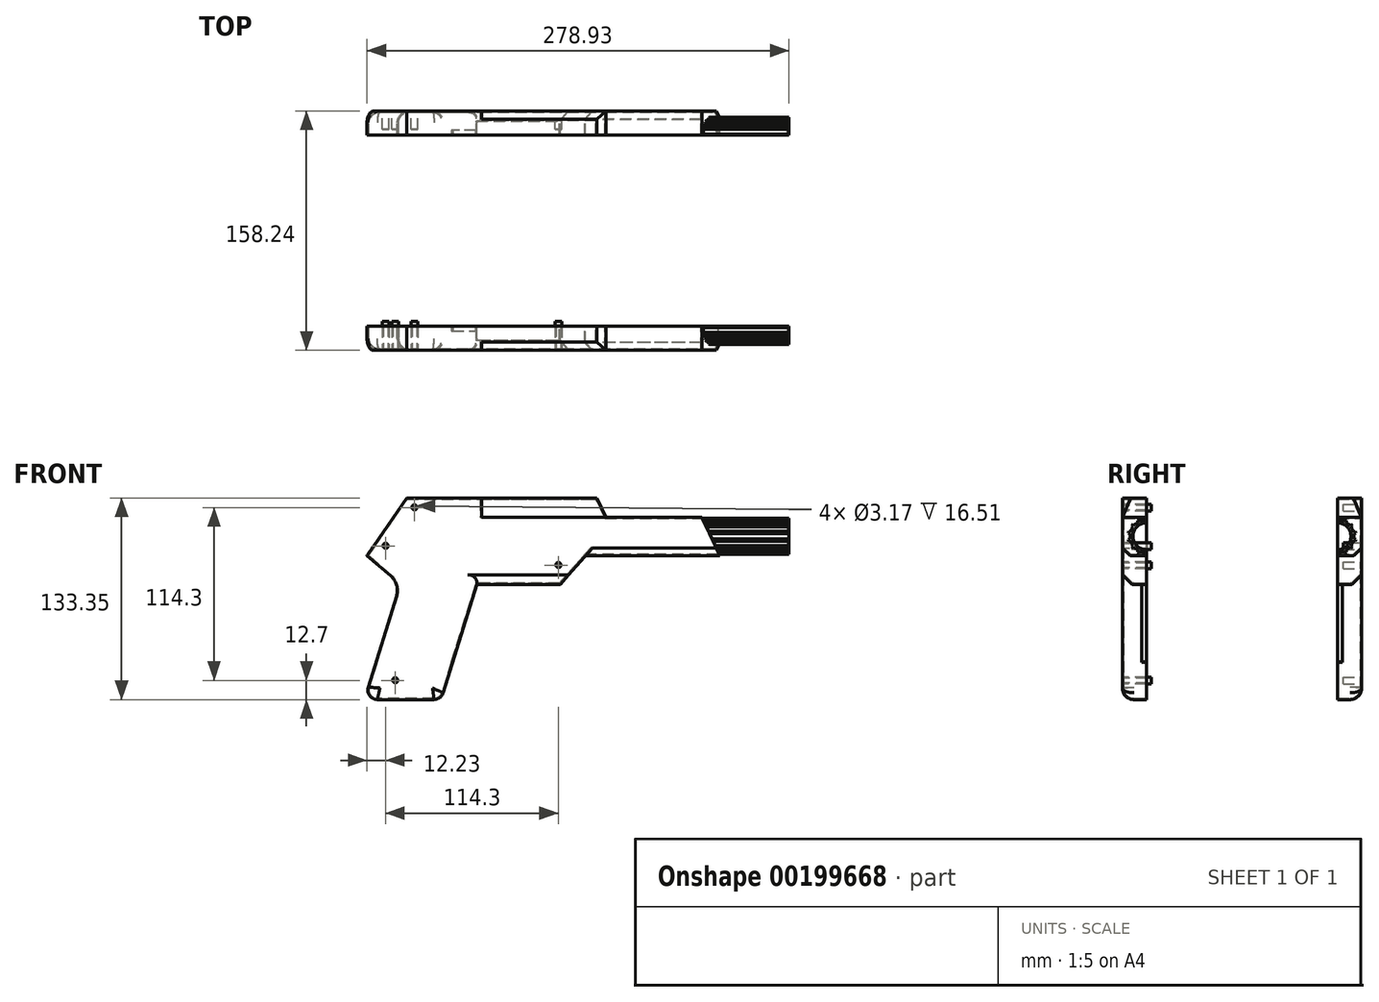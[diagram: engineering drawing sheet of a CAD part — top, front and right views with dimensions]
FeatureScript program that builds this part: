
annotation { "Feature Type Name" : "Feature", "Feature Type Description" : "" }
export const myFeature = defineFeature(function(context is Context, id is Id, definition is map)
    precondition{}
    {
        {
            var Q0;
            Q0=qCreatedBy(makeId("Front.planeOp"),FACE);
            var sketch = newSketch(context, id + "F0", { "sketchPlane" : qUnion([Q0])});
            skLineSegment(sketch, "E0", {"start": v(-151.93, 19.05) * mm, "end": v(-125.83, 57.15) * mm});
            skLineSegment(sketch, "E1", {"start": v(-125.83, 57.15) * mm, "end": v(0, 57.15) * mm});
            skLineSegment(sketch, "E2", {"start": v(0, 57.15) * mm, "end": v(6.06, 44.45) * mm});
            skLineSegment(sketch, "E3", {"start": v(6.06, 44.45) * mm, "end": v(69.56, 44.45) * mm});
            skLineSegment(sketch, "E4", {"start": v(69.56, 44.45) * mm, "end": v(81.44, 19.05) * mm});
            skLineSegment(sketch, "E5", {"start": v(81.44, 19.05) * mm, "end": v(-7.46, 19.05) * mm});
            skLineSegment(sketch, "E6", {"start": v(-7.46, 19.05) * mm, "end": v(-24.23, 0) * mm});
            skLineSegment(sketch, "E7", {"start": v(-24.23, 0) * mm, "end": v(-79.23, 0) * mm});
            skLineSegment(sketch, "E8", {"start": v(-79.23, 0) * mm, "end": v(-101.6, -71.74) * mm});
            skLineSegment(sketch, "E9", {"start": v(-107.67, -76.2) * mm, "end": v(-145.17, -76.2) * mm});
            skLineSegment(sketch, "E10", {"start": v(-151.23, -67.96) * mm, "end": v(-132.5, -7.92) * mm});
            skLineSegment(sketch, "E11", {"start": v(-136.29, 5.44) * mm, "end": v(-151.93, 19.05) * mm});
            skPoint(sketch, "E12.visualSharp", {"position": v(-130.03, 0) * mm});
            skArc(sketch, "E12.filletArc", {"start": v(-132.5, -7.92) * mm, "mid": v(-132.4, -0.67) * mm, "end": v(-136.29, 5.44) * mm});
            skPoint(sketch, "E13.visualSharp", {"position": v(-153.8, -76.2) * mm});
            skArc(sketch, "E13.filletArc", {"start": v(-151.23, -67.96) * mm, "mid": v(-150.28, -73.61) * mm, "end": v(-145.17, -76.2) * mm});
            skPoint(sketch, "E14.visualSharp", {"position": v(-103, -76.2) * mm});
            skArc(sketch, "E14.filletArc", {"start": v(-107.67, -76.2) * mm, "mid": v(-103.9, -74.97) * mm, "end": v(-101.6, -71.74) * mm});
            skSolve(sketch);
        }
        {
            var Q0;
            Q0=makeQuery(id+"F0.imprint","IMPRINT",FACE,{"disambiguationData":[TD([[makeQuery(id+"F0.imprint","IMPRINT",EDGE,{"derivedFrom":sQuery(id+"F0.wireOp",EDGE,"E0")}),-1.0]])]});
            extrude(context, id + "F1", {"entities" : qUnion([Q0]), "depth" : 31.75 * mm});
        }
        {
            var Q0;
            Q0=qCreatedBy(makeId("Right.planeOp"),FACE);
            var sketch = newSketch(context, id + "F2", { "sketchPlane" : qUnion([Q0])});
            skCircle(sketch, "E15", {"center": v(-15.88, 31.75) * mm, "radius": 10.8 * mm});
            skLineSegment(sketch, "E16.0", {"start": v(-31.75, 19.05) * mm, "end": v(0, 19.05) * mm});
            skSolve(sketch);
        }
        {
            var Q0;
            Q0=makeQuery(id+"F2.imprint","IMPRINT",FACE,{"disambiguationData":[TD([[makeQuery(id+"F2.imprint","IMPRINT",EDGE,{"derivedFrom":sQuery(id+"F2.wireOp",EDGE,"E15")}),1.0]])]});
            extrude(context, id + "F3", {"entities" : qUnion([Q0]), "operationType" : NewBodyOperationType.ADD, "depth" : 127 * mm});
        }
        {
            var Q0;
            Q0=makeQuery(id+"F3.opExtrude","CAP_FACE",FACE,{"disambiguationData":[OSD([sQuery(id+"F2.wireOp",EDGE,"E15")])],"isStart":false});
            var sketch = newSketch(context, id + "F4", { "sketchPlane" : qUnion([Q0])});
            skPoint(sketch, "E17.0", {"position": v(-15.88, 57.15) * mm});
            skLineSegment(sketch, "E18.0.0", {"start": v(0, 44.45) * mm, "end": v(0, 57.15) * mm});
            skLineSegment(sketch, "E18.0.1", {"start": v(0, 57.15) * mm, "end": v(-31.75, 57.15) * mm});
            skLineSegment(sketch, "E18.0.2", {"start": v(-31.75, 57.15) * mm, "end": v(-31.75, 44.45) * mm});
            skLineSegment(sketch, "E18.0.3", {"start": v(-31.75, 44.45) * mm, "end": v(0, 44.45) * mm});
            skLineSegment(sketch, "E19", {"start": v(-31.75, 44.45) * mm, "end": v(-26.23, 57.15) * mm});
            skLineSegment(sketch, "E20", {"start": v(-15.88, 57.15) * mm, "end": v(-15.88, 44.45) * mm});
            skLineSegment(sketch, "E21.MirrorCS", {"start": v(0, 44.45) * mm, "end": v(-5.52, 57.15) * mm});
            skSolve(sketch);
        }
        {
            var Q0;
            {var subQ0=sQuery(id+"F4.wireOp",EDGE,"E18.0.2");Q0=makeQuery(id+"F4.imprint","IMPRINT",FACE,{"disambiguationData":[TD([[makeQuery(id+"F4.imprint","IMPRINT",EDGE,{"derivedFrom":subQ0}),1.0]])]});}
            var Q1;
            {var subQ0=sQuery(id+"F4.wireOp",EDGE,"E18.0.0");Q1=makeQuery(id+"F4.imprint","IMPRINT",FACE,{"disambiguationData":[TD([[makeQuery(id+"F4.imprint","IMPRINT",EDGE,{"derivedFrom":subQ0}),1.0]])]});}
            extrude(context, id + "F5", {"entities" : qUnion([Q0, Q1]), "operationType" : NewBodyOperationType.REMOVE, "oppositeDirection" : true, "depth" : 203.2 * mm});
        }
        {
            var Q0;
            Q0=makeQuery(id+"F3.opExtrude","CAP_FACE",FACE,{"disambiguationData":[OSD([sQuery(id+"F2.wireOp",EDGE,"E15")])],"isStart":false});
            var sketch = newSketch(context, id + "F6", { "sketchPlane" : qUnion([Q0])});
            skPoint(sketch, "E22.0", {"position": v(0, 0) * mm});
            skLineSegment(sketch, "E23", {"start": v(-15.88, 31.75) * mm, "end": v(-15.88, 13.86) * mm});
            skLineSegment(sketch, "E24", {"start": v(-16.64, 20.98) * mm, "end": v(-16.64, 19.71) * mm});
            skLineSegment(sketch, "E25", {"start": v(-16.64, 19.71) * mm, "end": v(-15.88, 19.71) * mm});
            skLineSegment(sketch, "E26.MirrorCS", {"start": v(-15.11, 20.98) * mm, "end": v(-15.11, 19.71) * mm});
            skLineSegment(sketch, "E27.MirrorCS", {"start": v(-15.11, 19.71) * mm, "end": v(-15.88, 19.71) * mm});
            skLineSegment(sketch, "E28.1.0", {"start": v(-10.52, 22.38) * mm, "end": v(-9.97, 21.23) * mm});
            skLineSegment(sketch, "E28.1.1", {"start": v(-9.97, 21.23) * mm, "end": v(-10.65, 20.9) * mm});
            skLineSegment(sketch, "E28.1.2", {"start": v(-11.34, 20.57) * mm, "end": v(-10.65, 20.9) * mm});
            skLineSegment(sketch, "E28.1.3", {"start": v(-11.89, 21.72) * mm, "end": v(-11.34, 20.57) * mm});
            skLineSegment(sketch, "E28.2.0", {"start": v(-6.98, 25.63) * mm, "end": v(-5.99, 24.84) * mm});
            skLineSegment(sketch, "E28.2.1", {"start": v(-5.99, 24.84) * mm, "end": v(-6.46, 24.24) * mm});
            skLineSegment(sketch, "E28.2.2", {"start": v(-6.94, 23.65) * mm, "end": v(-6.46, 24.24) * mm});
            skLineSegment(sketch, "E28.2.3", {"start": v(-7.93, 24.44) * mm, "end": v(-6.94, 23.65) * mm});
            skLineSegment(sketch, "E28.3.0", {"start": v(-5.2, 30.1) * mm, "end": v(-3.97, 29.81) * mm});
            skLineSegment(sketch, "E28.3.1", {"start": v(-3.97, 29.81) * mm, "end": v(-4.14, 29.07) * mm});
            skLineSegment(sketch, "E28.3.2", {"start": v(-4.3, 28.33) * mm, "end": v(-4.14, 29.07) * mm});
            skLineSegment(sketch, "E28.3.3", {"start": v(-5.55, 28.61) * mm, "end": v(-4.3, 28.33) * mm});
            skLineSegment(sketch, "E28.4.0", {"start": v(-5.55, 34.89) * mm, "end": v(-4.3, 35.17) * mm});
            skLineSegment(sketch, "E28.4.1", {"start": v(-4.3, 35.17) * mm, "end": v(-4.14, 34.43) * mm});
            skLineSegment(sketch, "E28.4.2", {"start": v(-3.97, 33.69) * mm, "end": v(-4.14, 34.43) * mm});
            skLineSegment(sketch, "E28.4.3", {"start": v(-5.2, 33.4) * mm, "end": v(-3.97, 33.69) * mm});
            skLineSegment(sketch, "E28.5.0", {"start": v(-7.93, 39.06) * mm, "end": v(-6.94, 39.85) * mm});
            skLineSegment(sketch, "E28.5.1", {"start": v(-6.94, 39.85) * mm, "end": v(-6.46, 39.26) * mm});
            skLineSegment(sketch, "E28.5.2", {"start": v(-5.99, 38.66) * mm, "end": v(-6.46, 39.26) * mm});
            skLineSegment(sketch, "E28.5.3", {"start": v(-6.98, 37.87) * mm, "end": v(-5.99, 38.66) * mm});
            skLineSegment(sketch, "E28.6.0", {"start": v(-11.89, 41.78) * mm, "end": v(-11.34, 42.93) * mm});
            skLineSegment(sketch, "E28.6.1", {"start": v(-11.34, 42.93) * mm, "end": v(-10.65, 42.6) * mm});
            skLineSegment(sketch, "E28.6.2", {"start": v(-9.97, 42.27) * mm, "end": v(-10.65, 42.6) * mm});
            skLineSegment(sketch, "E28.6.3", {"start": v(-10.52, 41.12) * mm, "end": v(-9.97, 42.27) * mm});
            skLineSegment(sketch, "E28.7.0", {"start": v(-16.64, 42.52) * mm, "end": v(-16.64, 43.79) * mm});
            skLineSegment(sketch, "E28.7.1", {"start": v(-16.64, 43.79) * mm, "end": v(-15.88, 43.79) * mm});
            skLineSegment(sketch, "E28.7.2", {"start": v(-15.11, 43.79) * mm, "end": v(-15.88, 43.79) * mm});
            skLineSegment(sketch, "E28.7.3", {"start": v(-15.11, 42.52) * mm, "end": v(-15.11, 43.79) * mm});
            skLineSegment(sketch, "E28.8.0", {"start": v(-21.23, 41.12) * mm, "end": v(-21.78, 42.27) * mm});
            skLineSegment(sketch, "E28.8.1", {"start": v(-21.78, 42.27) * mm, "end": v(-21.1, 42.6) * mm});
            skLineSegment(sketch, "E28.8.2", {"start": v(-20.41, 42.93) * mm, "end": v(-21.1, 42.6) * mm});
            skLineSegment(sketch, "E28.8.3", {"start": v(-19.86, 41.78) * mm, "end": v(-20.41, 42.93) * mm});
            skLineSegment(sketch, "E28.9.0", {"start": v(-24.77, 37.87) * mm, "end": v(-25.76, 38.66) * mm});
            skLineSegment(sketch, "E28.9.1", {"start": v(-25.76, 38.66) * mm, "end": v(-25.29, 39.26) * mm});
            skLineSegment(sketch, "E28.9.2", {"start": v(-24.81, 39.85) * mm, "end": v(-25.29, 39.26) * mm});
            skLineSegment(sketch, "E28.9.3", {"start": v(-23.82, 39.06) * mm, "end": v(-24.81, 39.85) * mm});
            skLineSegment(sketch, "E28.10.0", {"start": v(-26.54, 33.4) * mm, "end": v(-27.78, 33.69) * mm});
            skLineSegment(sketch, "E28.10.1", {"start": v(-27.78, 33.69) * mm, "end": v(-27.61, 34.43) * mm});
            skLineSegment(sketch, "E28.10.2", {"start": v(-27.44, 35.17) * mm, "end": v(-27.61, 34.43) * mm});
            skLineSegment(sketch, "E28.10.3", {"start": v(-26.2, 34.89) * mm, "end": v(-27.44, 35.17) * mm});
            skLineSegment(sketch, "E28.11.0", {"start": v(-26.2, 28.61) * mm, "end": v(-27.44, 28.33) * mm});
            skLineSegment(sketch, "E28.11.1", {"start": v(-27.44, 28.33) * mm, "end": v(-27.61, 29.07) * mm});
            skLineSegment(sketch, "E28.11.2", {"start": v(-27.78, 29.81) * mm, "end": v(-27.61, 29.07) * mm});
            skLineSegment(sketch, "E28.11.3", {"start": v(-26.54, 30.1) * mm, "end": v(-27.78, 29.81) * mm});
            skLineSegment(sketch, "E28.12.0", {"start": v(-23.82, 24.44) * mm, "end": v(-24.81, 23.65) * mm});
            skLineSegment(sketch, "E28.12.1", {"start": v(-24.81, 23.65) * mm, "end": v(-25.29, 24.24) * mm});
            skLineSegment(sketch, "E28.12.2", {"start": v(-25.76, 24.84) * mm, "end": v(-25.29, 24.24) * mm});
            skLineSegment(sketch, "E28.12.3", {"start": v(-24.77, 25.63) * mm, "end": v(-25.76, 24.84) * mm});
            skLineSegment(sketch, "E28.13.0", {"start": v(-19.86, 21.72) * mm, "end": v(-20.41, 20.57) * mm});
            skLineSegment(sketch, "E28.13.1", {"start": v(-20.41, 20.57) * mm, "end": v(-21.1, 20.9) * mm});
            skLineSegment(sketch, "E28.13.2", {"start": v(-21.78, 21.23) * mm, "end": v(-21.1, 20.9) * mm});
            skLineSegment(sketch, "E28.13.3", {"start": v(-21.23, 22.38) * mm, "end": v(-21.78, 21.23) * mm});
            skPoint(sketch, "E28.center", {"position": v(-15.88, 31.75) * mm});
            skSolve(sketch);
        }
        {
            var Q0;
            Q0=makeQuery(id+"F1.opExtrude","CAP_EDGE",EDGE,{"disambiguationData":[OSD([sQuery(id+"F0.wireOp",EDGE,"E11")])],"isStart":false});
            fillet(context, id + "F7", {"entities" : qUnion([Q0]), "radius" : 7.62 * mm, "tangentPropagation" : true, "allowEdgeOverflow" : false});
        }
        {
            var Q0;
            Q0=makeQuery(id+"F1.opExtrude","CAP_EDGE",EDGE,{"disambiguationData":[OSD([sQuery(id+"F0.wireOp",EDGE,"E8")])],"isStart":true});
            fillet(context, id + "F8", {"entities" : qUnion([Q0]), "radius" : 7.62 * mm, "tangentPropagation" : true, "allowEdgeOverflow" : false});
        }
        {
            var Q0;
            Q0=makeQuery(id+"F1.opExtrude","CAP_EDGE",EDGE,{"disambiguationData":[OSD([sQuery(id+"F0.wireOp",EDGE,"E7")])],"isStart":false});
            var Q1;
            Q1=makeQuery(id+"F1.opExtrude","CAP_EDGE",EDGE,{"disambiguationData":[OSD([sQuery(id+"F0.wireOp",EDGE,"E7")])],"isStart":true});
            chamfer(context, id + "F9", {"entities" : qUnion([Q0, Q1]), "width" : 6.35 * mm, "tangentPropagation" : true});
        }
        {
            var Q0;
            Q0=makeQuery(id+"F1.opExtrude","CAP_EDGE",EDGE,{"disambiguationData":[OSD([sQuery(id+"F0.wireOp",EDGE,"E5")])],"isStart":false});
            var Q1;
            Q1=makeQuery(id+"F1.opExtrude","CAP_EDGE",EDGE,{"disambiguationData":[OSD([sQuery(id+"F0.wireOp",EDGE,"E5")])],"isStart":true});
            chamfer(context, id + "F10", {"entities" : qUnion([Q0, Q1]), "width" : 5.08 * mm, "tangentPropagation" : true});
        }
        {
            var Q0;
            {var subQ1=sQuery(id+"F6.wireOp",EDGE,"E28.6.0");Q0=makeQuery(id+"F6.imprint","IMPRINT",FACE,{"disambiguationData":[TD([[makeQuery(id+"F6.imprint","IMPRINT",EDGE,{"derivedFrom":subQ1}),-1.0]])]});}
            var Q1;
            {var subQ1=sQuery(id+"F6.wireOp",EDGE,"E28.7.0");Q1=makeQuery(id+"F6.imprint","IMPRINT",FACE,{"disambiguationData":[TD([[makeQuery(id+"F6.imprint","IMPRINT",EDGE,{"derivedFrom":subQ1}),-1.0]])]});}
            var Q2;
            {var subQ1=sQuery(id+"F6.wireOp",EDGE,"E28.8.0");Q2=makeQuery(id+"F6.imprint","IMPRINT",FACE,{"disambiguationData":[TD([[makeQuery(id+"F6.imprint","IMPRINT",EDGE,{"derivedFrom":subQ1}),-1.0]])]});}
            var Q3;
            {var subQ1=sQuery(id+"F6.wireOp",EDGE,"E28.9.0");Q3=makeQuery(id+"F6.imprint","IMPRINT",FACE,{"disambiguationData":[TD([[makeQuery(id+"F6.imprint","IMPRINT",EDGE,{"derivedFrom":subQ1}),-1.0]])]});}
            var Q4;
            {var subQ1=sQuery(id+"F6.wireOp",EDGE,"E28.10.0");Q4=makeQuery(id+"F6.imprint","IMPRINT",FACE,{"disambiguationData":[TD([[makeQuery(id+"F6.imprint","IMPRINT",EDGE,{"derivedFrom":subQ1}),-1.0]])]});}
            var Q5;
            {var subQ1=sQuery(id+"F6.wireOp",EDGE,"E28.11.0");Q5=makeQuery(id+"F6.imprint","IMPRINT",FACE,{"disambiguationData":[TD([[makeQuery(id+"F6.imprint","IMPRINT",EDGE,{"derivedFrom":subQ1}),-1.0]])]});}
            var Q6;
            {var subQ1=sQuery(id+"F6.wireOp",EDGE,"E28.4.0");Q6=makeQuery(id+"F6.imprint","IMPRINT",FACE,{"disambiguationData":[TD([[makeQuery(id+"F6.imprint","IMPRINT",EDGE,{"derivedFrom":subQ1}),-1.0]])]});}
            var Q7;
            {var subQ1=sQuery(id+"F6.wireOp",EDGE,"E28.5.0");Q7=makeQuery(id+"F6.imprint","IMPRINT",FACE,{"disambiguationData":[TD([[makeQuery(id+"F6.imprint","IMPRINT",EDGE,{"derivedFrom":subQ1}),-1.0]])]});}
            var Q8;
            {var subQ1=sQuery(id+"F6.wireOp",EDGE,"E28.3.0");Q8=makeQuery(id+"F6.imprint","IMPRINT",FACE,{"disambiguationData":[TD([[makeQuery(id+"F6.imprint","IMPRINT",EDGE,{"derivedFrom":subQ1}),-1.0]])]});}
            var Q9;
            {var subQ1=sQuery(id+"F6.wireOp",EDGE,"E28.2.0");Q9=makeQuery(id+"F6.imprint","IMPRINT",FACE,{"disambiguationData":[TD([[makeQuery(id+"F6.imprint","IMPRINT",EDGE,{"derivedFrom":subQ1}),-1.0]])]});}
            var Q10;
            {var subQ1=sQuery(id+"F6.wireOp",EDGE,"E28.1.0");Q10=makeQuery(id+"F6.imprint","IMPRINT",FACE,{"disambiguationData":[TD([[makeQuery(id+"F6.imprint","IMPRINT",EDGE,{"derivedFrom":subQ1}),-1.0]])]});}
            var Q11;
            {var subQ4=sQuery(id+"F6.wireOp",EDGE,"E26.MirrorCS");Q11=makeQuery(id+"F6.imprint","IMPRINT",FACE,{"disambiguationData":[TD([[makeQuery(id+"F6.imprint","IMPRINT",EDGE,{"derivedFrom":subQ4}),-1.0]])]});}
            var Q12;
            {var subQ4=sQuery(id+"F6.wireOp",EDGE,"E24");Q12=makeQuery(id+"F6.imprint","IMPRINT",FACE,{"disambiguationData":[TD([[makeQuery(id+"F6.imprint","IMPRINT",EDGE,{"derivedFrom":subQ4}),1.0]])]});}
            var Q13;
            {var subQ1=sQuery(id+"F6.wireOp",EDGE,"E28.13.0");Q13=makeQuery(id+"F6.imprint","IMPRINT",FACE,{"disambiguationData":[TD([[makeQuery(id+"F6.imprint","IMPRINT",EDGE,{"derivedFrom":subQ1}),-1.0]])]});}
            var Q14;
            {var subQ1=sQuery(id+"F6.wireOp",EDGE,"E28.12.0");Q14=makeQuery(id+"F6.imprint","IMPRINT",FACE,{"disambiguationData":[TD([[makeQuery(id+"F6.imprint","IMPRINT",EDGE,{"derivedFrom":subQ1}),-1.0]])]});}
            extrude(context, id + "F11", {"entities" : qUnion([Q0, Q1, Q2, Q3, Q4, Q5, Q6, Q7, Q8, Q9, Q10, Q11, Q12, Q13, Q14]), "operationType" : NewBodyOperationType.ADD, "oppositeDirection" : true, "depth" : 76.2 * mm});
        }
        {
            var Q0;
            Q0=makeQuery(id+"F1.opExtrude","SWEPT_BODY",BODY,{"disambiguationData":[OSD([sQuery(id+"F0.wireOp",EDGE,"E0"),sQuery(id+"F0.wireOp",EDGE,"E1"),sQuery(id+"F0.wireOp",EDGE,"E2"),sQuery(id+"F0.wireOp",EDGE,"E3"),sQuery(id+"F0.wireOp",EDGE,"E4"),sQuery(id+"F0.wireOp",EDGE,"E5"),sQuery(id+"F0.wireOp",EDGE,"E6"),sQuery(id+"F0.wireOp",EDGE,"E7"),sQuery(id+"F0.wireOp",EDGE,"E8"),sQuery(id+"F0.wireOp",EDGE,"E9"),sQuery(id+"F0.wireOp",EDGE,"E10"),sQuery(id+"F0.wireOp",EDGE,"E11"),sQuery(id+"F0.wireOp",EDGE,"E12.filletArc"),sQuery(id+"F0.wireOp",EDGE,"E13.filletArc"),sQuery(id+"F0.wireOp",EDGE,"E14.filletArc")])]});
            transform(context, id + "F12", {"entities" : qUnion([Q0]), "transformType" : TransformType.TRANSLATION_3D, "dx" : 0 * mm, "dy" : -126.5 * mm, "dz" : 0 * mm, "makeCopy" : true});
        }
        {
            var Q0;
            Q0=qCreatedBy(makeId("Right.planeOp"),FACE);
            cPlane(context, id + "F13", {"entities" : qUnion([Q0]), "cplaneType" : CPlaneType.OFFSET, "offset" : 203.2 * mm, "width" : 152.4 * mm, "height" : 152.4 * mm});
        }
        {
            var Q0;
            Q0=qCreatedBy(id+"F13.planeOp",FACE);
            var sketch = newSketch(context, id + "F14", { "sketchPlane" : qUnion([Q0])});
            skLineSegment(sketch, "E29.bottom", {"start": v(-15.88, 101.6) * mm, "end": v(-60.05, 101.6) * mm});
            skLineSegment(sketch, "E29.top", {"start": v(-15.87, -101.6) * mm, "end": v(-60.05, -101.6) * mm});
            skLineSegment(sketch, "E29.left", {"start": v(-15.88, 101.6) * mm, "end": v(-15.87, -101.6) * mm});
            skLineSegment(sketch, "E29.right", {"start": v(-60.05, 101.6) * mm, "end": v(-60.05, -101.6) * mm});
            skSolve(sketch);
        }
        {
            var Q0;
            Q0=makeQuery(id+"F14.imprint","IMPRINT",FACE,{"disambiguationData":[TD([[makeQuery(id+"F14.imprint","IMPRINT",EDGE,{"derivedFrom":sQuery(id+"F14.wireOp",EDGE,"E29.bottom")}),1.0]])]});
            extrude(context, id + "F15", {"entities" : qUnion([Q0]), "operationType" : NewBodyOperationType.REMOVE, "endBound" : BoundingType.THROUGH_ALL, "oppositeDirection" : true, "depth" : 25.4 * mm});
        }
        {
            var Q0;
            Q0=makeQuery(id+"F15.boolean.opBoolean","COPY",FACE,{"derivedFrom":makeQuery(id+"F15.opExtrude","SWEPT_FACE",FACE,{"disambiguationData":[OSD([sQuery(id+"F14.wireOp",EDGE,"E29.left")])]})});
            shell(context, id + "F16", {"entities" : qUnion([Q0]), "thickness" : 0.76 * mm});
        }
        {
            var Q0;
            Q0=qCreatedBy(id+"F13.planeOp",FACE);
            var sketch = newSketch(context, id + "F17", { "sketchPlane" : qUnion([Q0])});
            skLineSegment(sketch, "E30.bottom", {"start": v(-142.37, 71.47) * mm, "end": v(-104.36, 71.47) * mm});
            skLineSegment(sketch, "E30.top", {"start": v(-142.37, -104.52) * mm, "end": v(-104.36, -104.52) * mm});
            skLineSegment(sketch, "E30.left", {"start": v(-142.37, 71.47) * mm, "end": v(-142.37, -104.52) * mm});
            skLineSegment(sketch, "E30.right", {"start": v(-104.36, 71.47) * mm, "end": v(-104.36, -104.52) * mm});
            skLineSegment(sketch, "E31.0", {"start": v(-158.24, -68.58) * mm, "end": v(-158.24, 6.35) * mm});
            skSolve(sketch);
        }
        {
            var Q0;
            Q0=makeQuery(id+"F17.imprint","IMPRINT",FACE,{"disambiguationData":[TD([[makeQuery(id+"F17.imprint","IMPRINT",EDGE,{"derivedFrom":sQuery(id+"F17.wireOp",EDGE,"E30.bottom")}),-1.0]])]});
            extrude(context, id + "F18", {"entities" : qUnion([Q0]), "operationType" : NewBodyOperationType.REMOVE, "endBound" : BoundingType.THROUGH_ALL, "oppositeDirection" : true, "depth" : 25.4 * mm});
        }
        {
            var Q0;
            Q0=makeQuery(id+"F18.boolean.opBoolean","COPY",FACE,{"derivedFrom":makeQuery(id+"F18.opExtrude","SWEPT_FACE",FACE,{"disambiguationData":[OSD([sQuery(id+"F17.wireOp",EDGE,"E30.left")])]})});
            shell(context, id + "F19", {"entities" : qUnion([Q0]), "thickness" : 0.76 * mm});
        }
        {
            var Q0;
            Q0=makeQuery(id+"F12.opPattern","COPY",FACE,{"derivedFrom":makeQuery(id+"F1.opExtrude","SWEPT_FACE",FACE,{"disambiguationData":[OSD([sQuery(id+"F0.wireOp",EDGE,"E8")])]}),"instanceName":"1"});
            var sketch = newSketch(context, id + "F20", { "sketchPlane" : qUnion([Q0])});
            skLineSegment(sketch, "E32", {"start": v(-142.37, -77.57) * mm, "end": v(-145.54, -77.57) * mm});
            skLineSegment(sketch, "E33", {"start": v(-145.54, -77.57) * mm, "end": v(-145.54, -23.6) * mm});
            skLineSegment(sketch, "E34", {"start": v(-145.54, -23.6) * mm, "end": v(-142.37, -23.6) * mm});
            skLineSegment(sketch, "E35", {"start": v(-142.37, -23.6) * mm, "end": v(-142.37, -77.57) * mm});
            skSolve(sketch);
        }
        {
            var Q0;
            Q0=makeQuery(id+"F20.imprint","IMPRINT",FACE,{"disambiguationData":[TD([[makeQuery(id+"F20.imprint","IMPRINT",EDGE,{"derivedFrom":sQuery(id+"F20.wireOp",EDGE,"E32")}),-1.0]])]});
            extrude(context, id + "F21", {"entities" : qUnion([Q0]), "operationType" : NewBodyOperationType.REMOVE, "oppositeDirection" : true, "depth" : 6.35 * mm});
        }
        {
            var Q0;
            Q0=makeQuery(id+"F1.opExtrude","SWEPT_FACE",FACE,{"disambiguationData":[OSD([sQuery(id+"F0.wireOp",EDGE,"E8")])]});
            var sketch = newSketch(context, id + "F22", { "sketchPlane" : qUnion([Q0])});
            skLineSegment(sketch, "E36", {"start": v(-15.88, -23.6) * mm, "end": v(-12.7, -23.6) * mm});
            skLineSegment(sketch, "E37", {"start": v(-12.7, -23.6) * mm, "end": v(-12.7, -77.57) * mm});
            skLineSegment(sketch, "E38", {"start": v(-12.7, -77.57) * mm, "end": v(-15.88, -77.57) * mm});
            skLineSegment(sketch, "E39", {"start": v(-15.88, -77.57) * mm, "end": v(-15.88, -23.6) * mm});
            skSolve(sketch);
        }
        {
            var Q0;
            Q0=makeQuery(id+"F22.imprint","IMPRINT",FACE,{"disambiguationData":[TD([[makeQuery(id+"F22.imprint","IMPRINT",EDGE,{"derivedFrom":sQuery(id+"F22.wireOp",EDGE,"E36")}),-1.0]])]});
            extrude(context, id + "F23", {"entities" : qUnion([Q0]), "operationType" : NewBodyOperationType.REMOVE, "oppositeDirection" : true, "depth" : 6.35 * mm});
        }
        {
            var Q0;
            Q0=makeQuery(id+"F16.opShell","OFFSET_FACE",FACE,{"disambiguationData":[OSD([sQuery(id+"F0.wireOp",EDGE,"E0"),sQuery(id+"F0.wireOp",EDGE,"E1"),sQuery(id+"F0.wireOp",EDGE,"E2"),sQuery(id+"F0.wireOp",EDGE,"E3"),sQuery(id+"F0.wireOp",EDGE,"E4"),sQuery(id+"F0.wireOp",EDGE,"E5"),sQuery(id+"F0.wireOp",EDGE,"E6"),sQuery(id+"F0.wireOp",EDGE,"E7"),sQuery(id+"F0.wireOp",EDGE,"E8"),sQuery(id+"F0.wireOp",EDGE,"E9"),sQuery(id+"F0.wireOp",EDGE,"E10"),sQuery(id+"F0.wireOp",EDGE,"E11"),sQuery(id+"F0.wireOp",EDGE,"E12.filletArc"),sQuery(id+"F0.wireOp",EDGE,"E13.filletArc"),sQuery(id+"F0.wireOp",EDGE,"E14.filletArc")])]});
            var sketch = newSketch(context, id + "F24", { "sketchPlane" : qUnion([Q0])});
            skCircle(sketch, "E40", {"center": v(-120.65, 50.8) * mm, "radius": 2.22 * mm});
            skCircle(sketch, "E41", {"center": v(-139.7, 25.4) * mm, "radius": 2.22 * mm});
            skCircle(sketch, "E42", {"center": v(-133.35, -63.5) * mm, "radius": 2.22 * mm});
            skCircle(sketch, "E43", {"center": v(-25.4, 12.7) * mm, "radius": 2.22 * mm});
            skSolve(sketch);
        }
        {
            var Q0;
            Q0=makeQuery(id+"F24.imprint","IMPRINT",FACE,{"disambiguationData":[TD([[makeQuery(id+"F24.imprint","IMPRINT",EDGE,{"derivedFrom":sQuery(id+"F24.wireOp",EDGE,"E40")}),1.0]])]});
            var Q1;
            Q1=makeQuery(id+"F24.imprint","IMPRINT",FACE,{"disambiguationData":[TD([[makeQuery(id+"F24.imprint","IMPRINT",EDGE,{"derivedFrom":sQuery(id+"F24.wireOp",EDGE,"E41")}),1.0]])]});
            var Q2;
            Q2=makeQuery(id+"F24.imprint","IMPRINT",FACE,{"disambiguationData":[TD([[makeQuery(id+"F24.imprint","IMPRINT",EDGE,{"derivedFrom":sQuery(id+"F24.wireOp",EDGE,"E42")}),1.0]])]});
            var Q3;
            Q3=makeQuery(id+"F24.imprint","IMPRINT",FACE,{"disambiguationData":[TD([[makeQuery(id+"F24.imprint","IMPRINT",EDGE,{"derivedFrom":sQuery(id+"F24.wireOp",EDGE,"E43")}),1.0]])]});
            extrude(context, id + "F25", {"entities" : qUnion([Q0, Q1, Q2, Q3]), "operationType" : NewBodyOperationType.ADD, "depth" : 11.43 * mm});
        }
        {
            var Q0;
            {var subQ0=sQuery(id+"F2.wireOp",EDGE,"E15");Q0=makeQuery(id+"F11.boolean.opBoolean","MERGE",FACE,{"derivedFrom":[makeQuery(id+"F3.opExtrude","CAP_FACE",FACE,{"disambiguationData":[OSD([subQ0])],"isStart":false}),makeQuery(id+"F11.opExtrude","CAP_FACE",FACE,{"disambiguationData":[OSD([subQ0,sQuery(id+"F6.wireOp",EDGE,"E24"),sQuery(id+"F6.wireOp",EDGE,"E25"),sQuery(id+"F6.wireOp",EDGE,"E26.MirrorCS"),sQuery(id+"F6.wireOp",EDGE,"E27.MirrorCS")])],"isStart":true}),makeQuery(id+"F11.opExtrude","CAP_FACE",FACE,{"disambiguationData":[OSD([subQ0,sQuery(id+"F6.wireOp",EDGE,"E28.1.0"),sQuery(id+"F6.wireOp",EDGE,"E28.1.1"),sQuery(id+"F6.wireOp",EDGE,"E28.1.2"),sQuery(id+"F6.wireOp",EDGE,"E28.1.3")])],"isStart":true}),makeQuery(id+"F11.opExtrude","CAP_FACE",FACE,{"disambiguationData":[OSD([subQ0,sQuery(id+"F6.wireOp",EDGE,"E28.2.0"),sQuery(id+"F6.wireOp",EDGE,"E28.2.1"),sQuery(id+"F6.wireOp",EDGE,"E28.2.2"),sQuery(id+"F6.wireOp",EDGE,"E28.2.3")])],"isStart":true}),makeQuery(id+"F11.opExtrude","CAP_FACE",FACE,{"disambiguationData":[OSD([subQ0,sQuery(id+"F6.wireOp",EDGE,"E28.3.0"),sQuery(id+"F6.wireOp",EDGE,"E28.3.1"),sQuery(id+"F6.wireOp",EDGE,"E28.3.2"),sQuery(id+"F6.wireOp",EDGE,"E28.3.3")])],"isStart":true}),makeQuery(id+"F11.opExtrude","CAP_FACE",FACE,{"disambiguationData":[OSD([subQ0,sQuery(id+"F6.wireOp",EDGE,"E28.4.0"),sQuery(id+"F6.wireOp",EDGE,"E28.4.1"),sQuery(id+"F6.wireOp",EDGE,"E28.4.2"),sQuery(id+"F6.wireOp",EDGE,"E28.4.3")])],"isStart":true}),makeQuery(id+"F11.opExtrude","CAP_FACE",FACE,{"disambiguationData":[OSD([subQ0,sQuery(id+"F6.wireOp",EDGE,"E28.5.0"),sQuery(id+"F6.wireOp",EDGE,"E28.5.1"),sQuery(id+"F6.wireOp",EDGE,"E28.5.2"),sQuery(id+"F6.wireOp",EDGE,"E28.5.3")])],"isStart":true}),makeQuery(id+"F11.opExtrude","CAP_FACE",FACE,{"disambiguationData":[OSD([subQ0,sQuery(id+"F6.wireOp",EDGE,"E28.6.0"),sQuery(id+"F6.wireOp",EDGE,"E28.6.1"),sQuery(id+"F6.wireOp",EDGE,"E28.6.2"),sQuery(id+"F6.wireOp",EDGE,"E28.6.3")])],"isStart":true}),makeQuery(id+"F11.opExtrude","CAP_FACE",FACE,{"disambiguationData":[OSD([subQ0,sQuery(id+"F6.wireOp",EDGE,"E28.7.0"),sQuery(id+"F6.wireOp",EDGE,"E28.7.1"),sQuery(id+"F6.wireOp",EDGE,"E28.7.2"),sQuery(id+"F6.wireOp",EDGE,"E28.7.3")])],"isStart":true}),makeQuery(id+"F11.opExtrude","CAP_FACE",FACE,{"disambiguationData":[OSD([subQ0,sQuery(id+"F6.wireOp",EDGE,"E28.8.0"),sQuery(id+"F6.wireOp",EDGE,"E28.8.1"),sQuery(id+"F6.wireOp",EDGE,"E28.8.2"),sQuery(id+"F6.wireOp",EDGE,"E28.8.3")])],"isStart":true}),makeQuery(id+"F11.opExtrude","CAP_FACE",FACE,{"disambiguationData":[OSD([subQ0,sQuery(id+"F6.wireOp",EDGE,"E28.9.0"),sQuery(id+"F6.wireOp",EDGE,"E28.9.1"),sQuery(id+"F6.wireOp",EDGE,"E28.9.2"),sQuery(id+"F6.wireOp",EDGE,"E28.9.3")])],"isStart":true}),makeQuery(id+"F11.opExtrude","CAP_FACE",FACE,{"disambiguationData":[OSD([subQ0,sQuery(id+"F6.wireOp",EDGE,"E28.10.0"),sQuery(id+"F6.wireOp",EDGE,"E28.10.1"),sQuery(id+"F6.wireOp",EDGE,"E28.10.2"),sQuery(id+"F6.wireOp",EDGE,"E28.10.3")])],"isStart":true}),makeQuery(id+"F11.opExtrude","CAP_FACE",FACE,{"disambiguationData":[OSD([subQ0,sQuery(id+"F6.wireOp",EDGE,"E28.11.0"),sQuery(id+"F6.wireOp",EDGE,"E28.11.1"),sQuery(id+"F6.wireOp",EDGE,"E28.11.2"),sQuery(id+"F6.wireOp",EDGE,"E28.11.3")])],"isStart":true}),makeQuery(id+"F11.opExtrude","CAP_FACE",FACE,{"disambiguationData":[OSD([subQ0,sQuery(id+"F6.wireOp",EDGE,"E28.12.0"),sQuery(id+"F6.wireOp",EDGE,"E28.12.1"),sQuery(id+"F6.wireOp",EDGE,"E28.12.2"),sQuery(id+"F6.wireOp",EDGE,"E28.12.3")])],"isStart":true}),makeQuery(id+"F11.opExtrude","CAP_FACE",FACE,{"disambiguationData":[OSD([subQ0,sQuery(id+"F6.wireOp",EDGE,"E28.13.0"),sQuery(id+"F6.wireOp",EDGE,"E28.13.1"),sQuery(id+"F6.wireOp",EDGE,"E28.13.2"),sQuery(id+"F6.wireOp",EDGE,"E28.13.3")])],"isStart":true})]});}
            var sketch = newSketch(context, id + "F26", { "sketchPlane" : qUnion([Q0])});
            skCircle(sketch, "E44", {"center": v(-15.88, 31.75) * mm, "radius": 8.9 * mm});
            skSolve(sketch);
        }
        {
            var Q0;
            {var subQ0=sQuery(id+"F26.wireOp",EDGE,"E44");var subQ1=sQuery(id+"F2.wireOp",EDGE,"E15");var subQ2=makeQuery(id+"F15.boolean.opBoolean","INTERSECT",EDGE,{"derivedFrom":[makeQuery(id+"F11.boolean.opBoolean","MERGE",FACE,{"derivedFrom":[makeQuery(id+"F3.opExtrude","CAP_FACE",FACE,{"disambiguationData":[OSD([subQ1])],"isStart":false}),makeQuery(id+"F11.opExtrude","CAP_FACE",FACE,{"disambiguationData":[OSD([subQ1,sQuery(id+"F6.wireOp",EDGE,"E24"),sQuery(id+"F6.wireOp",EDGE,"E25"),sQuery(id+"F6.wireOp",EDGE,"E26.MirrorCS"),sQuery(id+"F6.wireOp",EDGE,"E27.MirrorCS")])],"isStart":true}),makeQuery(id+"F11.opExtrude","CAP_FACE",FACE,{"disambiguationData":[OSD([subQ1,sQuery(id+"F6.wireOp",EDGE,"E28.1.0"),sQuery(id+"F6.wireOp",EDGE,"E28.1.1"),sQuery(id+"F6.wireOp",EDGE,"E28.1.2"),sQuery(id+"F6.wireOp",EDGE,"E28.1.3")])],"isStart":true}),makeQuery(id+"F11.opExtrude","CAP_FACE",FACE,{"disambiguationData":[OSD([subQ1,sQuery(id+"F6.wireOp",EDGE,"E28.2.0"),sQuery(id+"F6.wireOp",EDGE,"E28.2.1"),sQuery(id+"F6.wireOp",EDGE,"E28.2.2"),sQuery(id+"F6.wireOp",EDGE,"E28.2.3")])],"isStart":true}),makeQuery(id+"F11.opExtrude","CAP_FACE",FACE,{"disambiguationData":[OSD([subQ1,sQuery(id+"F6.wireOp",EDGE,"E28.3.0"),sQuery(id+"F6.wireOp",EDGE,"E28.3.1"),sQuery(id+"F6.wireOp",EDGE,"E28.3.2"),sQuery(id+"F6.wireOp",EDGE,"E28.3.3")])],"isStart":true}),makeQuery(id+"F11.opExtrude","CAP_FACE",FACE,{"disambiguationData":[OSD([subQ1,sQuery(id+"F6.wireOp",EDGE,"E28.4.0"),sQuery(id+"F6.wireOp",EDGE,"E28.4.1"),sQuery(id+"F6.wireOp",EDGE,"E28.4.2"),sQuery(id+"F6.wireOp",EDGE,"E28.4.3")])],"isStart":true}),makeQuery(id+"F11.opExtrude","CAP_FACE",FACE,{"disambiguationData":[OSD([subQ1,sQuery(id+"F6.wireOp",EDGE,"E28.5.0"),sQuery(id+"F6.wireOp",EDGE,"E28.5.1"),sQuery(id+"F6.wireOp",EDGE,"E28.5.2"),sQuery(id+"F6.wireOp",EDGE,"E28.5.3")])],"isStart":true}),makeQuery(id+"F11.opExtrude","CAP_FACE",FACE,{"disambiguationData":[OSD([subQ1,sQuery(id+"F6.wireOp",EDGE,"E28.6.0"),sQuery(id+"F6.wireOp",EDGE,"E28.6.1"),sQuery(id+"F6.wireOp",EDGE,"E28.6.2"),sQuery(id+"F6.wireOp",EDGE,"E28.6.3")])],"isStart":true}),makeQuery(id+"F11.opExtrude","CAP_FACE",FACE,{"disambiguationData":[OSD([subQ1,sQuery(id+"F6.wireOp",EDGE,"E28.7.0"),sQuery(id+"F6.wireOp",EDGE,"E28.7.1"),sQuery(id+"F6.wireOp",EDGE,"E28.7.2"),sQuery(id+"F6.wireOp",EDGE,"E28.7.3")])],"isStart":true}),makeQuery(id+"F11.opExtrude","CAP_FACE",FACE,{"disambiguationData":[OSD([subQ1,sQuery(id+"F6.wireOp",EDGE,"E28.8.0"),sQuery(id+"F6.wireOp",EDGE,"E28.8.1"),sQuery(id+"F6.wireOp",EDGE,"E28.8.2"),sQuery(id+"F6.wireOp",EDGE,"E28.8.3")])],"isStart":true}),makeQuery(id+"F11.opExtrude","CAP_FACE",FACE,{"disambiguationData":[OSD([subQ1,sQuery(id+"F6.wireOp",EDGE,"E28.9.0"),sQuery(id+"F6.wireOp",EDGE,"E28.9.1"),sQuery(id+"F6.wireOp",EDGE,"E28.9.2"),sQuery(id+"F6.wireOp",EDGE,"E28.9.3")])],"isStart":true}),makeQuery(id+"F11.opExtrude","CAP_FACE",FACE,{"disambiguationData":[OSD([subQ1,sQuery(id+"F6.wireOp",EDGE,"E28.10.0"),sQuery(id+"F6.wireOp",EDGE,"E28.10.1"),sQuery(id+"F6.wireOp",EDGE,"E28.10.2"),sQuery(id+"F6.wireOp",EDGE,"E28.10.3")])],"isStart":true}),makeQuery(id+"F11.opExtrude","CAP_FACE",FACE,{"disambiguationData":[OSD([subQ1,sQuery(id+"F6.wireOp",EDGE,"E28.11.0"),sQuery(id+"F6.wireOp",EDGE,"E28.11.1"),sQuery(id+"F6.wireOp",EDGE,"E28.11.2"),sQuery(id+"F6.wireOp",EDGE,"E28.11.3")])],"isStart":true}),makeQuery(id+"F11.opExtrude","CAP_FACE",FACE,{"disambiguationData":[OSD([subQ1,sQuery(id+"F6.wireOp",EDGE,"E28.12.0"),sQuery(id+"F6.wireOp",EDGE,"E28.12.1"),sQuery(id+"F6.wireOp",EDGE,"E28.12.2"),sQuery(id+"F6.wireOp",EDGE,"E28.12.3")])],"isStart":true}),makeQuery(id+"F11.opExtrude","CAP_FACE",FACE,{"disambiguationData":[OSD([subQ1,sQuery(id+"F6.wireOp",EDGE,"E28.13.0"),sQuery(id+"F6.wireOp",EDGE,"E28.13.1"),sQuery(id+"F6.wireOp",EDGE,"E28.13.2"),sQuery(id+"F6.wireOp",EDGE,"E28.13.3")])],"isStart":true})]}),makeQuery(id+"F15.opExtrude","SWEPT_FACE",FACE,{"disambiguationData":[OSD([sQuery(id+"F14.wireOp",EDGE,"E29.left")])]})]});var subQ3=makeQuery(id+"F26.imprint","INTERSECT",VERTEX,{"disambiguationData":[OD(0.0)],"derivedFrom":[subQ2,subQ0]});Q0=makeQuery(id+"F26.imprint","IMPRINT",FACE,{"disambiguationData":[TD([[makeQuery(id+"F26.imprint","IMPRINT",EDGE,{"disambiguationData":[TD([[subQ3,-1.0]])],"derivedFrom":subQ0}),1.0]])]});}
            extrude(context, id + "F27", {"entities" : qUnion([Q0]), "operationType" : NewBodyOperationType.REMOVE, "oppositeDirection" : true, "depth" : 25.4 * mm});
        }
        {
            var Q0;
            Q0=makeQuery(id+"F12.opPattern","COPY",FACE,{"derivedFrom":makeQuery(id+"F1.opExtrude","CAP_FACE",FACE,{"disambiguationData":[OSD([sQuery(id+"F0.wireOp",EDGE,"E0"),sQuery(id+"F0.wireOp",EDGE,"E1"),sQuery(id+"F0.wireOp",EDGE,"E2"),sQuery(id+"F0.wireOp",EDGE,"E3"),sQuery(id+"F0.wireOp",EDGE,"E4"),sQuery(id+"F0.wireOp",EDGE,"E5"),sQuery(id+"F0.wireOp",EDGE,"E6"),sQuery(id+"F0.wireOp",EDGE,"E7"),sQuery(id+"F0.wireOp",EDGE,"E8"),sQuery(id+"F0.wireOp",EDGE,"E9"),sQuery(id+"F0.wireOp",EDGE,"E10"),sQuery(id+"F0.wireOp",EDGE,"E11"),sQuery(id+"F0.wireOp",EDGE,"E12.filletArc"),sQuery(id+"F0.wireOp",EDGE,"E13.filletArc"),sQuery(id+"F0.wireOp",EDGE,"E14.filletArc")])],"isStart":false}),"instanceName":"1"});
            var sketch = newSketch(context, id + "F28", { "sketchPlane" : qUnion([Q0])});
            skCircle(sketch, "E45.0", {"center": v(-120.65, 50.8) * mm, "radius": 2.22 * mm});
            skCircle(sketch, "E46.0", {"center": v(-139.7, 25.4) * mm, "radius": 2.22 * mm});
            skCircle(sketch, "E47.0", {"center": v(-133.35, -63.5) * mm, "radius": 2.22 * mm});
            skCircle(sketch, "E48.0", {"center": v(-25.4, 12.7) * mm, "radius": 2.22 * mm});
            skSolve(sketch);
        }
        {
            var Q0;
            Q0=makeQuery(id+"F28.imprint","IMPRINT",FACE,{"disambiguationData":[TD([[makeQuery(id+"F28.imprint","IMPRINT",EDGE,{"derivedFrom":sQuery(id+"F28.wireOp",EDGE,"E45.0")}),1.0]])]});
            var Q1;
            Q1=makeQuery(id+"F28.imprint","IMPRINT",FACE,{"disambiguationData":[TD([[makeQuery(id+"F28.imprint","IMPRINT",EDGE,{"derivedFrom":sQuery(id+"F28.wireOp",EDGE,"E46.0")}),1.0]])]});
            var Q2;
            Q2=makeQuery(id+"F28.imprint","IMPRINT",FACE,{"disambiguationData":[TD([[makeQuery(id+"F28.imprint","IMPRINT",EDGE,{"derivedFrom":sQuery(id+"F28.wireOp",EDGE,"E48.0")}),1.0]])]});
            var Q3;
            Q3=makeQuery(id+"F28.imprint","IMPRINT",FACE,{"disambiguationData":[TD([[makeQuery(id+"F28.imprint","IMPRINT",EDGE,{"derivedFrom":sQuery(id+"F28.wireOp",EDGE,"E47.0")}),1.0]])]});
            extrude(context, id + "F29", {"entities" : qUnion([Q0, Q1, Q2, Q3]), "operationType" : NewBodyOperationType.ADD, "oppositeDirection" : true, "depth" : 19.05 * mm});
        }
        {
            var Q0;
            {var subQ0=sQuery(id+"F2.wireOp",EDGE,"E15");Q0=makeQuery(id+"F12.opPattern","COPY",FACE,{"derivedFrom":makeQuery(id+"F11.boolean.opBoolean","MERGE",FACE,{"derivedFrom":[makeQuery(id+"F3.opExtrude","CAP_FACE",FACE,{"disambiguationData":[OSD([subQ0])],"isStart":false}),makeQuery(id+"F11.opExtrude","CAP_FACE",FACE,{"disambiguationData":[OSD([subQ0,sQuery(id+"F6.wireOp",EDGE,"E24"),sQuery(id+"F6.wireOp",EDGE,"E25"),sQuery(id+"F6.wireOp",EDGE,"E26.MirrorCS"),sQuery(id+"F6.wireOp",EDGE,"E27.MirrorCS")])],"isStart":true}),makeQuery(id+"F11.opExtrude","CAP_FACE",FACE,{"disambiguationData":[OSD([subQ0,sQuery(id+"F6.wireOp",EDGE,"E28.1.0"),sQuery(id+"F6.wireOp",EDGE,"E28.1.1"),sQuery(id+"F6.wireOp",EDGE,"E28.1.2"),sQuery(id+"F6.wireOp",EDGE,"E28.1.3")])],"isStart":true}),makeQuery(id+"F11.opExtrude","CAP_FACE",FACE,{"disambiguationData":[OSD([subQ0,sQuery(id+"F6.wireOp",EDGE,"E28.2.0"),sQuery(id+"F6.wireOp",EDGE,"E28.2.1"),sQuery(id+"F6.wireOp",EDGE,"E28.2.2"),sQuery(id+"F6.wireOp",EDGE,"E28.2.3")])],"isStart":true}),makeQuery(id+"F11.opExtrude","CAP_FACE",FACE,{"disambiguationData":[OSD([subQ0,sQuery(id+"F6.wireOp",EDGE,"E28.3.0"),sQuery(id+"F6.wireOp",EDGE,"E28.3.1"),sQuery(id+"F6.wireOp",EDGE,"E28.3.2"),sQuery(id+"F6.wireOp",EDGE,"E28.3.3")])],"isStart":true}),makeQuery(id+"F11.opExtrude","CAP_FACE",FACE,{"disambiguationData":[OSD([subQ0,sQuery(id+"F6.wireOp",EDGE,"E28.4.0"),sQuery(id+"F6.wireOp",EDGE,"E28.4.1"),sQuery(id+"F6.wireOp",EDGE,"E28.4.2"),sQuery(id+"F6.wireOp",EDGE,"E28.4.3")])],"isStart":true}),makeQuery(id+"F11.opExtrude","CAP_FACE",FACE,{"disambiguationData":[OSD([subQ0,sQuery(id+"F6.wireOp",EDGE,"E28.5.0"),sQuery(id+"F6.wireOp",EDGE,"E28.5.1"),sQuery(id+"F6.wireOp",EDGE,"E28.5.2"),sQuery(id+"F6.wireOp",EDGE,"E28.5.3")])],"isStart":true}),makeQuery(id+"F11.opExtrude","CAP_FACE",FACE,{"disambiguationData":[OSD([subQ0,sQuery(id+"F6.wireOp",EDGE,"E28.6.0"),sQuery(id+"F6.wireOp",EDGE,"E28.6.1"),sQuery(id+"F6.wireOp",EDGE,"E28.6.2"),sQuery(id+"F6.wireOp",EDGE,"E28.6.3")])],"isStart":true}),makeQuery(id+"F11.opExtrude","CAP_FACE",FACE,{"disambiguationData":[OSD([subQ0,sQuery(id+"F6.wireOp",EDGE,"E28.7.0"),sQuery(id+"F6.wireOp",EDGE,"E28.7.1"),sQuery(id+"F6.wireOp",EDGE,"E28.7.2"),sQuery(id+"F6.wireOp",EDGE,"E28.7.3")])],"isStart":true}),makeQuery(id+"F11.opExtrude","CAP_FACE",FACE,{"disambiguationData":[OSD([subQ0,sQuery(id+"F6.wireOp",EDGE,"E28.8.0"),sQuery(id+"F6.wireOp",EDGE,"E28.8.1"),sQuery(id+"F6.wireOp",EDGE,"E28.8.2"),sQuery(id+"F6.wireOp",EDGE,"E28.8.3")])],"isStart":true}),makeQuery(id+"F11.opExtrude","CAP_FACE",FACE,{"disambiguationData":[OSD([subQ0,sQuery(id+"F6.wireOp",EDGE,"E28.9.0"),sQuery(id+"F6.wireOp",EDGE,"E28.9.1"),sQuery(id+"F6.wireOp",EDGE,"E28.9.2"),sQuery(id+"F6.wireOp",EDGE,"E28.9.3")])],"isStart":true}),makeQuery(id+"F11.opExtrude","CAP_FACE",FACE,{"disambiguationData":[OSD([subQ0,sQuery(id+"F6.wireOp",EDGE,"E28.10.0"),sQuery(id+"F6.wireOp",EDGE,"E28.10.1"),sQuery(id+"F6.wireOp",EDGE,"E28.10.2"),sQuery(id+"F6.wireOp",EDGE,"E28.10.3")])],"isStart":true}),makeQuery(id+"F11.opExtrude","CAP_FACE",FACE,{"disambiguationData":[OSD([subQ0,sQuery(id+"F6.wireOp",EDGE,"E28.11.0"),sQuery(id+"F6.wireOp",EDGE,"E28.11.1"),sQuery(id+"F6.wireOp",EDGE,"E28.11.2"),sQuery(id+"F6.wireOp",EDGE,"E28.11.3")])],"isStart":true}),makeQuery(id+"F11.opExtrude","CAP_FACE",FACE,{"disambiguationData":[OSD([subQ0,sQuery(id+"F6.wireOp",EDGE,"E28.12.0"),sQuery(id+"F6.wireOp",EDGE,"E28.12.1"),sQuery(id+"F6.wireOp",EDGE,"E28.12.2"),sQuery(id+"F6.wireOp",EDGE,"E28.12.3")])],"isStart":true}),makeQuery(id+"F11.opExtrude","CAP_FACE",FACE,{"disambiguationData":[OSD([subQ0,sQuery(id+"F6.wireOp",EDGE,"E28.13.0"),sQuery(id+"F6.wireOp",EDGE,"E28.13.1"),sQuery(id+"F6.wireOp",EDGE,"E28.13.2"),sQuery(id+"F6.wireOp",EDGE,"E28.13.3")])],"isStart":true})]}),"instanceName":"1"});}
            var sketch = newSketch(context, id + "F30", { "sketchPlane" : qUnion([Q0])});
            skCircle(sketch, "E49", {"center": v(-142.37, 31.75) * mm, "radius": 8.9 * mm});
            skSolve(sketch);
        }
        {
            var Q0;
            {var subQ0=sQuery(id+"F30.wireOp",EDGE,"E49");var subQ1=sQuery(id+"F2.wireOp",EDGE,"E15");var subQ2=makeQuery(id+"F18.boolean.opBoolean","INTERSECT",EDGE,{"derivedFrom":[makeQuery(id+"F12.opPattern","COPY",FACE,{"derivedFrom":makeQuery(id+"F11.boolean.opBoolean","MERGE",FACE,{"derivedFrom":[makeQuery(id+"F3.opExtrude","CAP_FACE",FACE,{"disambiguationData":[OSD([subQ1])],"isStart":false}),makeQuery(id+"F11.opExtrude","CAP_FACE",FACE,{"disambiguationData":[OSD([subQ1,sQuery(id+"F6.wireOp",EDGE,"E24"),sQuery(id+"F6.wireOp",EDGE,"E25"),sQuery(id+"F6.wireOp",EDGE,"E26.MirrorCS"),sQuery(id+"F6.wireOp",EDGE,"E27.MirrorCS")])],"isStart":true}),makeQuery(id+"F11.opExtrude","CAP_FACE",FACE,{"disambiguationData":[OSD([subQ1,sQuery(id+"F6.wireOp",EDGE,"E28.1.0"),sQuery(id+"F6.wireOp",EDGE,"E28.1.1"),sQuery(id+"F6.wireOp",EDGE,"E28.1.2"),sQuery(id+"F6.wireOp",EDGE,"E28.1.3")])],"isStart":true}),makeQuery(id+"F11.opExtrude","CAP_FACE",FACE,{"disambiguationData":[OSD([subQ1,sQuery(id+"F6.wireOp",EDGE,"E28.2.0"),sQuery(id+"F6.wireOp",EDGE,"E28.2.1"),sQuery(id+"F6.wireOp",EDGE,"E28.2.2"),sQuery(id+"F6.wireOp",EDGE,"E28.2.3")])],"isStart":true}),makeQuery(id+"F11.opExtrude","CAP_FACE",FACE,{"disambiguationData":[OSD([subQ1,sQuery(id+"F6.wireOp",EDGE,"E28.3.0"),sQuery(id+"F6.wireOp",EDGE,"E28.3.1"),sQuery(id+"F6.wireOp",EDGE,"E28.3.2"),sQuery(id+"F6.wireOp",EDGE,"E28.3.3")])],"isStart":true}),makeQuery(id+"F11.opExtrude","CAP_FACE",FACE,{"disambiguationData":[OSD([subQ1,sQuery(id+"F6.wireOp",EDGE,"E28.4.0"),sQuery(id+"F6.wireOp",EDGE,"E28.4.1"),sQuery(id+"F6.wireOp",EDGE,"E28.4.2"),sQuery(id+"F6.wireOp",EDGE,"E28.4.3")])],"isStart":true}),makeQuery(id+"F11.opExtrude","CAP_FACE",FACE,{"disambiguationData":[OSD([subQ1,sQuery(id+"F6.wireOp",EDGE,"E28.5.0"),sQuery(id+"F6.wireOp",EDGE,"E28.5.1"),sQuery(id+"F6.wireOp",EDGE,"E28.5.2"),sQuery(id+"F6.wireOp",EDGE,"E28.5.3")])],"isStart":true}),makeQuery(id+"F11.opExtrude","CAP_FACE",FACE,{"disambiguationData":[OSD([subQ1,sQuery(id+"F6.wireOp",EDGE,"E28.6.0"),sQuery(id+"F6.wireOp",EDGE,"E28.6.1"),sQuery(id+"F6.wireOp",EDGE,"E28.6.2"),sQuery(id+"F6.wireOp",EDGE,"E28.6.3")])],"isStart":true}),makeQuery(id+"F11.opExtrude","CAP_FACE",FACE,{"disambiguationData":[OSD([subQ1,sQuery(id+"F6.wireOp",EDGE,"E28.7.0"),sQuery(id+"F6.wireOp",EDGE,"E28.7.1"),sQuery(id+"F6.wireOp",EDGE,"E28.7.2"),sQuery(id+"F6.wireOp",EDGE,"E28.7.3")])],"isStart":true}),makeQuery(id+"F11.opExtrude","CAP_FACE",FACE,{"disambiguationData":[OSD([subQ1,sQuery(id+"F6.wireOp",EDGE,"E28.8.0"),sQuery(id+"F6.wireOp",EDGE,"E28.8.1"),sQuery(id+"F6.wireOp",EDGE,"E28.8.2"),sQuery(id+"F6.wireOp",EDGE,"E28.8.3")])],"isStart":true}),makeQuery(id+"F11.opExtrude","CAP_FACE",FACE,{"disambiguationData":[OSD([subQ1,sQuery(id+"F6.wireOp",EDGE,"E28.9.0"),sQuery(id+"F6.wireOp",EDGE,"E28.9.1"),sQuery(id+"F6.wireOp",EDGE,"E28.9.2"),sQuery(id+"F6.wireOp",EDGE,"E28.9.3")])],"isStart":true}),makeQuery(id+"F11.opExtrude","CAP_FACE",FACE,{"disambiguationData":[OSD([subQ1,sQuery(id+"F6.wireOp",EDGE,"E28.10.0"),sQuery(id+"F6.wireOp",EDGE,"E28.10.1"),sQuery(id+"F6.wireOp",EDGE,"E28.10.2"),sQuery(id+"F6.wireOp",EDGE,"E28.10.3")])],"isStart":true}),makeQuery(id+"F11.opExtrude","CAP_FACE",FACE,{"disambiguationData":[OSD([subQ1,sQuery(id+"F6.wireOp",EDGE,"E28.11.0"),sQuery(id+"F6.wireOp",EDGE,"E28.11.1"),sQuery(id+"F6.wireOp",EDGE,"E28.11.2"),sQuery(id+"F6.wireOp",EDGE,"E28.11.3")])],"isStart":true}),makeQuery(id+"F11.opExtrude","CAP_FACE",FACE,{"disambiguationData":[OSD([subQ1,sQuery(id+"F6.wireOp",EDGE,"E28.12.0"),sQuery(id+"F6.wireOp",EDGE,"E28.12.1"),sQuery(id+"F6.wireOp",EDGE,"E28.12.2"),sQuery(id+"F6.wireOp",EDGE,"E28.12.3")])],"isStart":true}),makeQuery(id+"F11.opExtrude","CAP_FACE",FACE,{"disambiguationData":[OSD([subQ1,sQuery(id+"F6.wireOp",EDGE,"E28.13.0"),sQuery(id+"F6.wireOp",EDGE,"E28.13.1"),sQuery(id+"F6.wireOp",EDGE,"E28.13.2"),sQuery(id+"F6.wireOp",EDGE,"E28.13.3")])],"isStart":true})]}),"instanceName":"1"}),makeQuery(id+"F18.opExtrude","SWEPT_FACE",FACE,{"disambiguationData":[OSD([sQuery(id+"F17.wireOp",EDGE,"E30.left")])]})]});var subQ3=makeQuery(id+"F30.imprint","INTERSECT",VERTEX,{"disambiguationData":[OD(0.0)],"derivedFrom":[subQ2,subQ0]});Q0=makeQuery(id+"F30.imprint","IMPRINT",FACE,{"disambiguationData":[TD([[makeQuery(id+"F30.imprint","IMPRINT",EDGE,{"disambiguationData":[TD([[subQ3,1.0]])],"derivedFrom":subQ0}),1.0]])]});}
            extrude(context, id + "F31", {"entities" : qUnion([Q0]), "operationType" : NewBodyOperationType.REMOVE, "oppositeDirection" : true, "depth" : 25.4 * mm});
        }
        {
            var Q0;
            Q0=makeQuery(id+"F12.opPattern","COPY",FACE,{"derivedFrom":makeQuery(id+"F1.opExtrude","CAP_FACE",FACE,{"disambiguationData":[OSD([sQuery(id+"F0.wireOp",EDGE,"E0"),sQuery(id+"F0.wireOp",EDGE,"E1"),sQuery(id+"F0.wireOp",EDGE,"E2"),sQuery(id+"F0.wireOp",EDGE,"E3"),sQuery(id+"F0.wireOp",EDGE,"E4"),sQuery(id+"F0.wireOp",EDGE,"E5"),sQuery(id+"F0.wireOp",EDGE,"E6"),sQuery(id+"F0.wireOp",EDGE,"E7"),sQuery(id+"F0.wireOp",EDGE,"E8"),sQuery(id+"F0.wireOp",EDGE,"E9"),sQuery(id+"F0.wireOp",EDGE,"E10"),sQuery(id+"F0.wireOp",EDGE,"E11"),sQuery(id+"F0.wireOp",EDGE,"E12.filletArc"),sQuery(id+"F0.wireOp",EDGE,"E13.filletArc"),sQuery(id+"F0.wireOp",EDGE,"E14.filletArc")])],"isStart":false}),"instanceName":"1"});
            var sketch = newSketch(context, id + "F32", { "sketchPlane" : qUnion([Q0])});
            skCircle(sketch, "E50.0", {"center": v(-120.65, 50.8) * mm, "radius": 2.22 * mm});
            skCircle(sketch, "E51.0", {"center": v(-139.7, 25.4) * mm, "radius": 2.22 * mm});
            skCircle(sketch, "E52.0", {"center": v(-133.35, -63.5) * mm, "radius": 2.22 * mm});
            skCircle(sketch, "E53.0", {"center": v(-25.4, 12.7) * mm, "radius": 2.22 * mm});
            skCircle(sketch, "E54", {"center": v(-120.65, 50.8) * mm, "radius": 1.59 * mm});
            skCircle(sketch, "E55", {"center": v(-139.7, 25.4) * mm, "radius": 1.59 * mm});
            skCircle(sketch, "E56", {"center": v(-133.35, -63.5) * mm, "radius": 1.59 * mm});
            skCircle(sketch, "E57", {"center": v(-25.4, 12.7) * mm, "radius": 1.59 * mm});
            skSolve(sketch);
        }
        {
            var Q0;
            Q0=makeQuery(id+"F32.imprint","IMPRINT",FACE,{"disambiguationData":[TD([[makeQuery(id+"F32.imprint","IMPRINT",EDGE,{"derivedFrom":sQuery(id+"F32.wireOp",EDGE,"E54")}),1.0]])]});
            var Q1;
            Q1=makeQuery(id+"F32.imprint","IMPRINT",FACE,{"disambiguationData":[TD([[makeQuery(id+"F32.imprint","IMPRINT",EDGE,{"derivedFrom":sQuery(id+"F32.wireOp",EDGE,"E55")}),1.0]])]});
            var Q2;
            Q2=makeQuery(id+"F32.imprint","IMPRINT",FACE,{"disambiguationData":[TD([[makeQuery(id+"F32.imprint","IMPRINT",EDGE,{"derivedFrom":sQuery(id+"F32.wireOp",EDGE,"E56")}),1.0]])]});
            var Q3;
            Q3=makeQuery(id+"F32.imprint","IMPRINT",FACE,{"disambiguationData":[TD([[makeQuery(id+"F32.imprint","IMPRINT",EDGE,{"derivedFrom":sQuery(id+"F32.wireOp",EDGE,"E57")}),1.0]])]});
            extrude(context, id + "F33", {"entities" : qUnion([Q0, Q1, Q2, Q3]), "operationType" : NewBodyOperationType.REMOVE, "oppositeDirection" : true, "depth" : 16.5 * mm});
        }
    });
